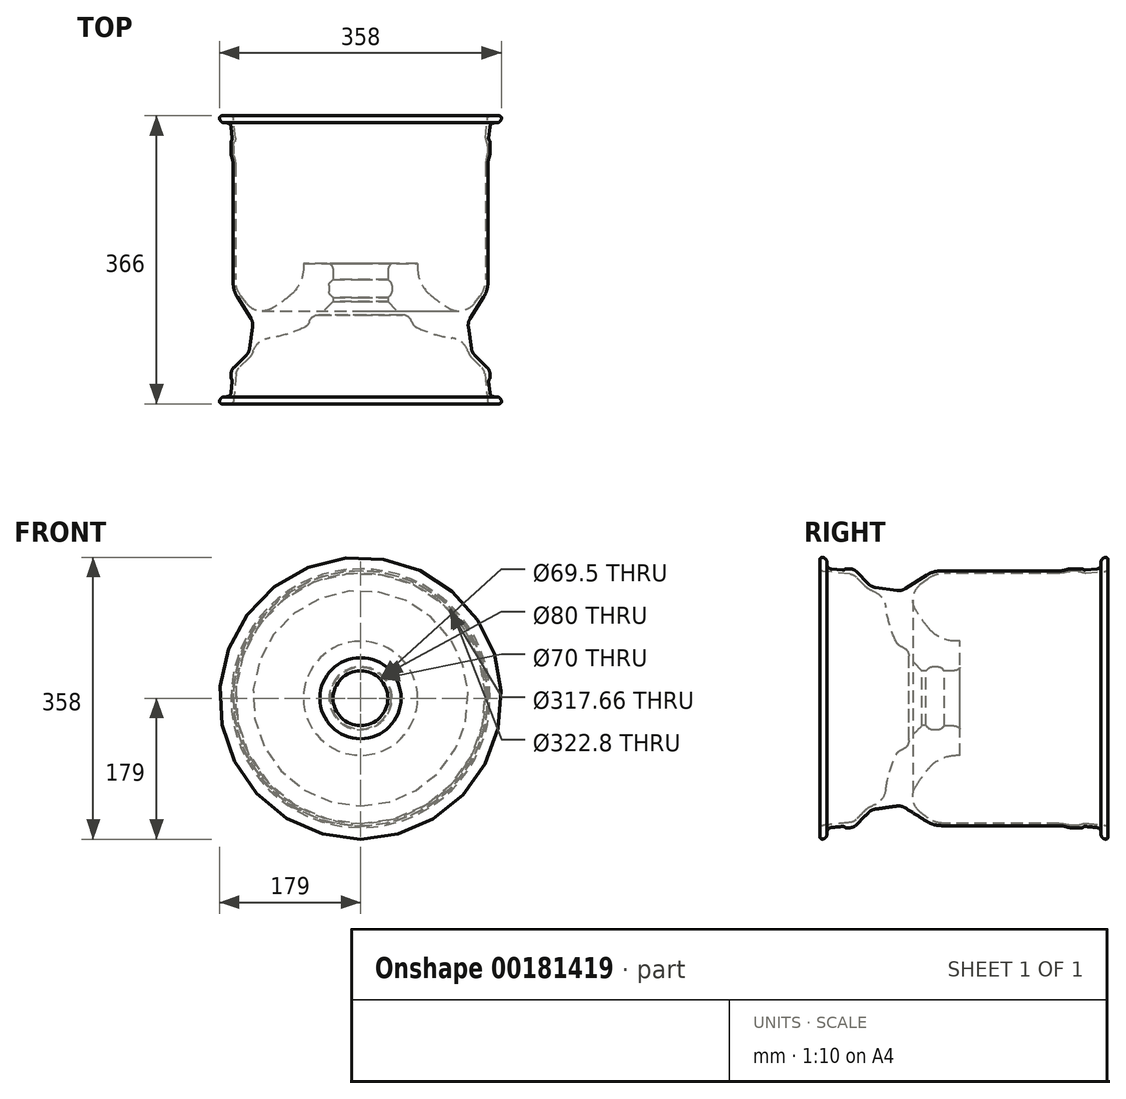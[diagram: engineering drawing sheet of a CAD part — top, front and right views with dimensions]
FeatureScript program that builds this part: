
annotation { "Feature Type Name" : "Feature", "Feature Type Description" : "" }
export const myFeature = defineFeature(function(context is Context, id is Id, definition is map)
    precondition{}
    {
        {
            var Q0;
            Q0=qCreatedBy(makeId("Right.planeOp"),FACE);
            var sketch = newSketch(context, id + "F0", { "sketchPlane" : qUnion([Q0])});
            skLineSegment(sketch, "E0", {"start": v(183, 165.33) * mm, "end": v(183, 176) * mm});
            skArc(sketch, "E1", {"start": v(183, 176) * mm, "mid": v(181.96, 178.27) * mm, "end": v(179.57, 178.97) * mm});
            skArc(sketch, "E2", {"start": v(179.57, 178.97) * mm, "mid": v(175.59, 176.8) * mm, "end": v(174, 172.54) * mm});
            skLineSegment(sketch, "E3", {"start": v(174, 172.54) * mm, "end": v(174, 170.25) * mm});
            skArc(sketch, "E4", {"start": v(174, 170.25) * mm, "mid": v(172.45, 166.23) * mm, "end": v(168.6, 164.28) * mm});
            skLineSegment(sketch, "E5", {"start": v(168.6, 164.28) * mm, "end": v(154.4, 162.85) * mm});
            skLineSegment(sketch, "E6", {"start": v(150.15, 164.4) * mm, "end": v(135.15, 164.4) * mm});
            skLineSegment(sketch, "E7", {"start": v(135.15, 161.4) * mm, "end": v(144.73, 161.4) * mm});
            skLineSegment(sketch, "E8", {"start": v(154.8, 158.87) * mm, "end": v(179.4, 161.35) * mm});
            skArc(sketch, "E9.filletArc", {"start": v(179.4, 161.35) * mm, "mid": v(181.97, 162.65) * mm, "end": v(183, 165.33) * mm});
            skPoint(sketch, "E10", {"position": v(174, 164.82) * mm});
            skArc(sketch, "E11", {"start": v(150.15, 164.4) * mm, "mid": v(150.72, 164.29) * mm, "end": v(151.2, 163.97) * mm});
            skArc(sketch, "E12", {"start": v(151.2, 163.97) * mm, "mid": v(152.68, 163.06) * mm, "end": v(154.4, 162.85) * mm});
            skArc(sketch, "E13", {"start": v(154.8, 158.87) * mm, "mid": v(152.25, 159.02) * mm, "end": v(149.88, 159.97) * mm});
            skArc(sketch, "E14", {"start": v(149.88, 159.97) * mm, "mid": v(147.4, 161.04) * mm, "end": v(144.73, 161.4) * mm});
            skArc(sketch, "E15.filletArc", {"start": v(135.15, 161.4) * mm, "mid": v(133.43, 161.25) * mm, "end": v(131.75, 160.8) * mm});
            skArc(sketch, "E16", {"start": v(131.75, 160.8) * mm, "mid": v(126.22, 159.33) * mm, "end": v(120.52, 158.83) * mm});
            skArc(sketch, "E17", {"start": v(135.15, 164.4) * mm, "mid": v(132.9, 164.2) * mm, "end": v(130.73, 163.62) * mm});
            skArc(sketch, "E18", {"start": v(130.73, 163.62) * mm, "mid": v(125.7, 162.28) * mm, "end": v(120.52, 161.83) * mm});
            skLineSegment(sketch, "E19", {"start": v(120.52, 161.83) * mm, "end": v(-28.68, 161.83) * mm});
            skLineSegment(sketch, "E20", {"start": v(120.52, 158.83) * mm, "end": v(-25, 158.83) * mm});
            skArc(sketch, "E21", {"start": v(-25, 158.83) * mm, "mid": v(-36.16, 157) * mm, "end": v(-46.16, 151.7) * mm});
            skLineSegment(sketch, "E22", {"start": v(-46.16, 151.7) * mm, "end": v(-55.12, 144.91) * mm});
            skArc(sketch, "E23", {"start": v(-55.12, 144.91) * mm, "mid": v(-64.56, 129.7) * mm, "end": v(-61.4, 112.07) * mm});
            skArc(sketch, "E24", {"start": v(-61.4, 112.07) * mm, "mid": v(-53.3, 99.82) * mm, "end": v(-44.22, 88.27) * mm});
            skArc(sketch, "E25", {"start": v(-44.22, 88.27) * mm, "mid": v(-28.84, 76.63) * mm, "end": v(-10, 72.5) * mm});
            skLineSegment(sketch, "E26", {"start": v(-10, 72.5) * mm, "end": v(-10, 72.5) * mm});
            skLineSegment(sketch, "E27", {"start": v(-10, 72.5) * mm, "end": v(-5, 72.5) * mm});
            skLineSegment(sketch, "E28", {"start": v(-5, 72.5) * mm, "end": v(-5, 39) * mm});
            skArc(sketch, "E29", {"start": v(-13, 35) * mm, "mid": v(-8.53, 36.06) * mm, "end": v(-5, 39) * mm});
            skLineSegment(sketch, "E30", {"start": v(-13, 35) * mm, "end": v(-25, 35) * mm});
            skLineSegment(sketch, "E31", {"start": v(-32.49, 40) * mm, "end": v(-40.51, 40) * mm});
            skLineSegment(sketch, "E32", {"start": v(-44.76, 38.24) * mm, "end": v(-48.25, 34.75) * mm});
            skLineSegment(sketch, "E33", {"start": v(-48.25, 34.75) * mm, "end": v(-53.25, 34.75) * mm});
            skLineSegment(sketch, "E34", {"start": v(-53.25, 34.75) * mm, "end": v(-70, 51.5) * mm});
            skLineSegment(sketch, "E35", {"start": v(-70, 51.5) * mm, "end": v(-70, 53.5) * mm});
            skArc(sketch, "E36.filletArc", {"start": v(-40.51, 40) * mm, "mid": v(-42.81, 39.54) * mm, "end": v(-44.76, 38.24) * mm});
            skArc(sketch, "E37", {"start": v(-137.21, 154.28) * mm, "mid": v(-140.6, 156.71) * mm, "end": v(-144.6, 157.85) * mm});
            skLineSegment(sketch, "E38", {"start": v(-144.6, 157.85) * mm, "end": v(-179.4, 161.35) * mm});
            skArc(sketch, "E39", {"start": v(-179.4, 161.35) * mm, "mid": v(-181.97, 162.65) * mm, "end": v(-183, 165.33) * mm});
            skLineSegment(sketch, "E40", {"start": v(-183, 165.33) * mm, "end": v(-183, 176) * mm});
            skArc(sketch, "E41", {"start": v(-183, 176) * mm, "mid": v(-181.96, 178.27) * mm, "end": v(-179.57, 178.97) * mm});
            skArc(sketch, "E42", {"start": v(-179.57, 178.97) * mm, "mid": v(-175.59, 176.8) * mm, "end": v(-174, 172.54) * mm});
            skLineSegment(sketch, "E43", {"start": v(-174, 172.54) * mm, "end": v(-174, 170.25) * mm});
            skArc(sketch, "E44", {"start": v(-174, 170.25) * mm, "mid": v(-172.45, 166.23) * mm, "end": v(-168.6, 164.28) * mm});
            skLineSegment(sketch, "E45", {"start": v(-168.6, 164.28) * mm, "end": v(-154.4, 162.85) * mm});
            skArc(sketch, "E46", {"start": v(-154.4, 162.85) * mm, "mid": v(-152.68, 163.06) * mm, "end": v(-151.2, 163.97) * mm});
            skArc(sketch, "E47", {"start": v(-151.2, 163.97) * mm, "mid": v(-150.72, 164.29) * mm, "end": v(-150.15, 164.4) * mm});
            skLineSegment(sketch, "E48", {"start": v(-150.15, 164.4) * mm, "end": v(-145.15, 164.4) * mm});
            skArc(sketch, "E49", {"start": v(-145.15, 164.4) * mm, "mid": v(-140.49, 163.46) * mm, "end": v(-136.56, 160.77) * mm});
            skArc(sketch, "E50", {"start": v(-85.34, 136.98) * mm, "mid": v(-79.75, 137.18) * mm, "end": v(-74.58, 139.29) * mm});
            skLineSegment(sketch, "E51", {"start": v(-74.58, 139.29) * mm, "end": v(-47.33, 156.45) * mm});
            skArc(sketch, "E52", {"start": v(-47.33, 156.45) * mm, "mid": v(-38.39, 160.46) * mm, "end": v(-28.68, 161.83) * mm});
            skPoint(sketch, "E53", {"position": v(-174, 164.82) * mm});
            skCircle(sketch, "E54", {"center": v(-166, 172.06) * mm, "radius": 8 * mm, "construction": true});
            skCircle(sketch, "E55", {"center": v(166, 172.06) * mm, "radius": 8 * mm, "construction": true});
            skLineSegment(sketch, "E56", {"start": v(-94.56, 136.82) * mm, "end": v(-78.96, 136.82) * mm, "construction": true});
            skArc(sketch, "E57", {"start": v(-99.35, 116.18) * mm, "mid": v(-94.35, 93.17) * mm, "end": v(-85.8, 71.24) * mm});
            skArc(sketch, "E58.filletArc", {"start": v(-99.35, 116.18) * mm, "mid": v(-105, 128.89) * mm, "end": v(-116.55, 136.62) * mm});
            skLineSegment(sketch, "E59", {"start": v(-136.56, 160.77) * mm, "end": v(-121.65, 145.47) * mm});
            skLineSegment(sketch, "E60", {"start": v(-125.23, 141.98) * mm, "end": v(-137.21, 154.28) * mm});
            skLineSegment(sketch, "E61", {"start": v(-112.41, 140.79) * mm, "end": v(-85.34, 136.98) * mm});
            skArc(sketch, "E62.filletArc", {"start": v(-121.65, 145.47) * mm, "mid": v(-117.42, 142.36) * mm, "end": v(-112.41, 140.79) * mm});
            skArc(sketch, "E63.filletArc", {"start": v(-125.23, 141.98) * mm, "mid": v(-121.22, 138.76) * mm, "end": v(-116.55, 136.62) * mm});
            skArc(sketch, "E64.filletArc", {"start": v(-70, 53.5) * mm, "mid": v(-72.36, 60.64) * mm, "end": v(-78.5, 64.98) * mm});
            skLineSegment(sketch, "E65", {"start": v(-28.24, 38.24) * mm, "end": v(-25, 35) * mm});
            skArc(sketch, "E66.filletArc", {"start": v(-28.24, 38.24) * mm, "mid": v(-30.19, 39.54) * mm, "end": v(-32.49, 40) * mm});
            skArc(sketch, "E67.filletArc", {"start": v(-85.8, 71.24) * mm, "mid": v(-82.8, 67.34) * mm, "end": v(-78.5, 64.98) * mm});
            skLineSegment(sketch, "E68", {"start": v(-128.12, 0) * mm, "end": v(133.22, 0) * mm, "construction": true});
            skSolve(sketch);
        }
        {
            var Q0;
            Q0 = qSketchRegion(id + "F0", true);
            var Q1;
            Q1=sQuery(id+"F0.wireOp",EDGE,"E68");
            revolve(context, id + "F1", {"entities" : qUnion([Q0]), "axis" : qUnion([Q1]), "revolveType" : RevolveType.FULL});
        }
    });
